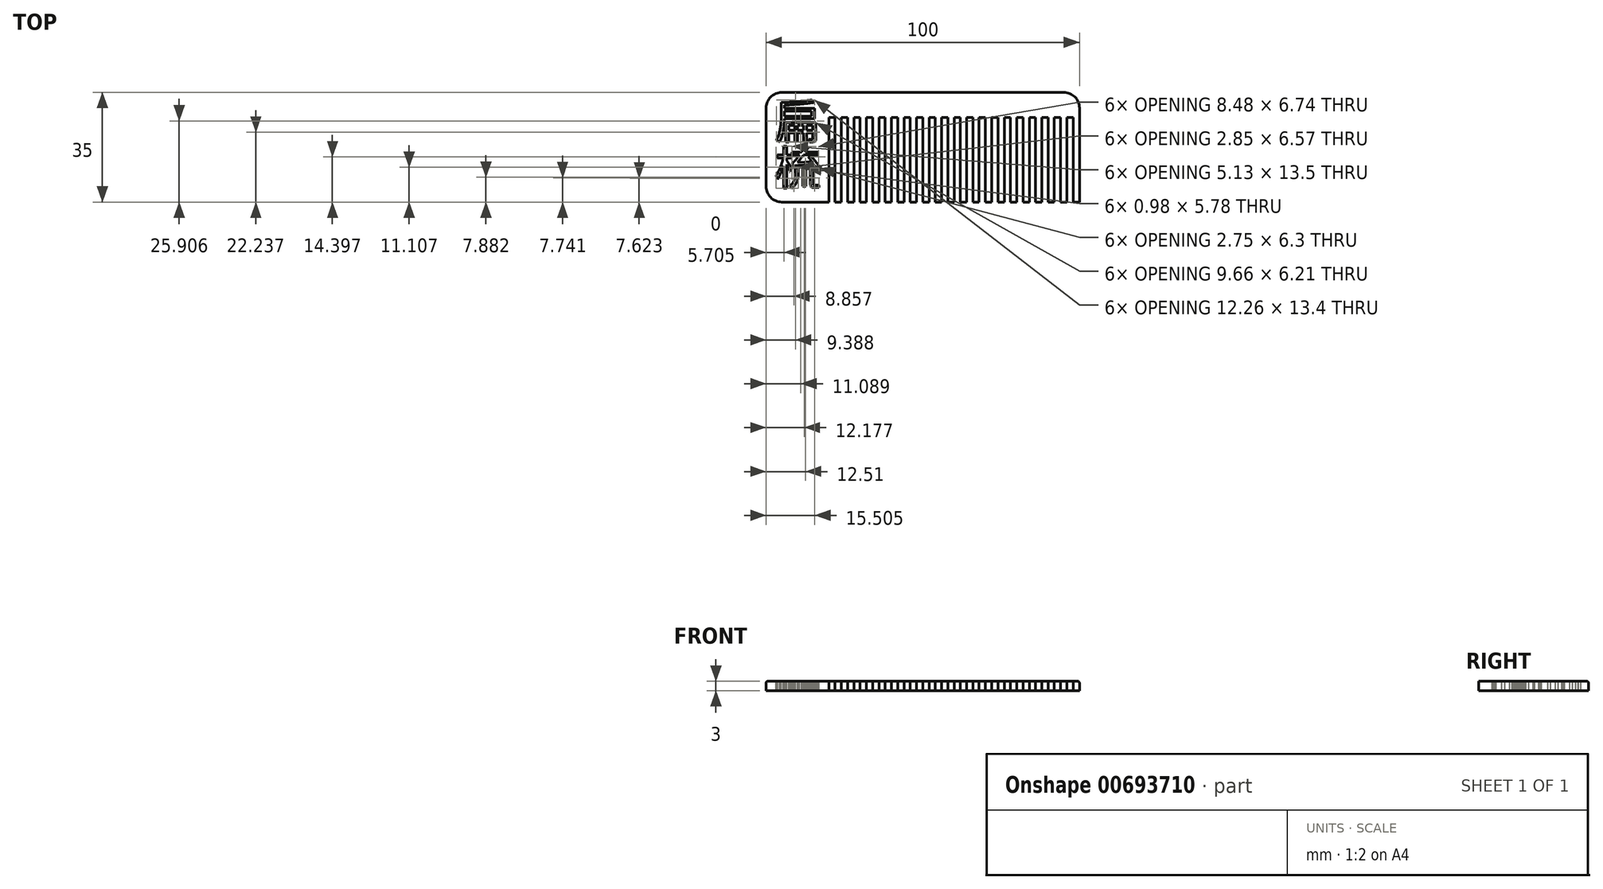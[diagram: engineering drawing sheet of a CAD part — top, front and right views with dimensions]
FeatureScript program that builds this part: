
annotation { "Feature Type Name" : "Feature", "Feature Type Description" : "" }
export const myFeature = defineFeature(function(context is Context, id is Id, definition is map)
    precondition{}
    {
        {
            var Q0;
            Q0=qCreatedBy(makeId("Top.planeOp"),FACE);
            var sketch = newSketch(context, id + "F0", { "sketchPlane" : qUnion([Q0])});
            skLineSegment(sketch, "E0.bottom", {"start": v(50, 17.5) * mm, "end": v(-50, 17.5) * mm});
            skLineSegment(sketch, "E0.top", {"start": v(50, -17.5) * mm, "end": v(-50, -17.5) * mm});
            skLineSegment(sketch, "E0.left", {"start": v(50, 17.5) * mm, "end": v(50, -17.5) * mm});
            skLineSegment(sketch, "E0.right", {"start": v(-50, 17.5) * mm, "end": v(-50, -17.5) * mm});
            skPoint(sketch, "E0.middle", {"position": v(0, 0) * mm});
            skSolve(sketch);
        }
        {
            var Q0;
            Q0 = qSketchRegion(id + "F0", true);
            extrude(context, id + "F1", {"entities" : qUnion([Q0]), "depth" : 3 * mm, "offsetDistance" : 25 * mm});
        }
        {
            var Q0;
            Q0=makeQuery(id+"F1.opExtrude","CAP_FACE",FACE,{"disambiguationData":[OSD([sQuery(id+"F0.wireOp",EDGE,"E0.bottom"),sQuery(id+"F0.wireOp",EDGE,"E0.top"),sQuery(id+"F0.wireOp",EDGE,"E0.left"),sQuery(id+"F0.wireOp",EDGE,"E0.right")])],"isStart":false});
            var sketch = newSketch(context, id + "F2", { "sketchPlane" : qUnion([Q0])});
            skLineSegment(sketch, "E1.bottom", {"start": v(48, 9.5) * mm, "end": v(46, 9.5) * mm});
            skLineSegment(sketch, "E1.top", {"start": v(48, -17.5) * mm, "end": v(46, -17.5) * mm});
            skLineSegment(sketch, "E1.left", {"start": v(48, 9.5) * mm, "end": v(48, -17.5) * mm});
            skLineSegment(sketch, "E1.right", {"start": v(46, 9.5) * mm, "end": v(46, -17.5) * mm});
            skLineSegment(sketch, "E2.1.0.0", {"start": v(42, 9.5) * mm, "end": v(42, -17.5) * mm});
            skLineSegment(sketch, "E2.1.0.1", {"start": v(44, 9.5) * mm, "end": v(44, -17.5) * mm});
            skLineSegment(sketch, "E2.1.0.2", {"start": v(44, -17.5) * mm, "end": v(42, -17.5) * mm});
            skLineSegment(sketch, "E2.1.0.3", {"start": v(44, 9.5) * mm, "end": v(42, 9.5) * mm});
            skLineSegment(sketch, "E2.2.0.0", {"start": v(38, 9.5) * mm, "end": v(38, -17.5) * mm});
            skLineSegment(sketch, "E2.2.0.1", {"start": v(40, 9.5) * mm, "end": v(40, -17.5) * mm});
            skLineSegment(sketch, "E2.2.0.2", {"start": v(40, -17.5) * mm, "end": v(38, -17.5) * mm});
            skLineSegment(sketch, "E2.2.0.3", {"start": v(40, 9.5) * mm, "end": v(38, 9.5) * mm});
            skLineSegment(sketch, "E2.3.0.0", {"start": v(34, 9.5) * mm, "end": v(34, -17.5) * mm});
            skLineSegment(sketch, "E2.3.0.1", {"start": v(36, 9.5) * mm, "end": v(36, -17.5) * mm});
            skLineSegment(sketch, "E2.3.0.2", {"start": v(36, -17.5) * mm, "end": v(34, -17.5) * mm});
            skLineSegment(sketch, "E2.3.0.3", {"start": v(36, 9.5) * mm, "end": v(34, 9.5) * mm});
            skLineSegment(sketch, "E2.4.0.0", {"start": v(30, 9.5) * mm, "end": v(30, -17.5) * mm});
            skLineSegment(sketch, "E2.4.0.1", {"start": v(32, 9.5) * mm, "end": v(32, -17.5) * mm});
            skLineSegment(sketch, "E2.4.0.2", {"start": v(32, -17.5) * mm, "end": v(30, -17.5) * mm});
            skLineSegment(sketch, "E2.4.0.3", {"start": v(32, 9.5) * mm, "end": v(30, 9.5) * mm});
            skLineSegment(sketch, "E2.5.0.0", {"start": v(26, 9.5) * mm, "end": v(26, -17.5) * mm});
            skLineSegment(sketch, "E2.5.0.1", {"start": v(28, 9.5) * mm, "end": v(28, -17.5) * mm});
            skLineSegment(sketch, "E2.5.0.2", {"start": v(28, -17.5) * mm, "end": v(26, -17.5) * mm});
            skLineSegment(sketch, "E2.5.0.3", {"start": v(28, 9.5) * mm, "end": v(26, 9.5) * mm});
            skLineSegment(sketch, "E2.6.0.0", {"start": v(22, 9.5) * mm, "end": v(22, -17.5) * mm});
            skLineSegment(sketch, "E2.6.0.1", {"start": v(24, 9.5) * mm, "end": v(24, -17.5) * mm});
            skLineSegment(sketch, "E2.6.0.2", {"start": v(24, -17.5) * mm, "end": v(22, -17.5) * mm});
            skLineSegment(sketch, "E2.6.0.3", {"start": v(24, 9.5) * mm, "end": v(22, 9.5) * mm});
            skLineSegment(sketch, "E2.7.0.0", {"start": v(18, 9.5) * mm, "end": v(18, -17.5) * mm});
            skLineSegment(sketch, "E2.7.0.1", {"start": v(20, 9.5) * mm, "end": v(20, -17.5) * mm});
            skLineSegment(sketch, "E2.7.0.2", {"start": v(20, -17.5) * mm, "end": v(18, -17.5) * mm});
            skLineSegment(sketch, "E2.7.0.3", {"start": v(20, 9.5) * mm, "end": v(18, 9.5) * mm});
            skLineSegment(sketch, "E2.8.0.0", {"start": v(14, 9.5) * mm, "end": v(14, -17.5) * mm});
            skLineSegment(sketch, "E2.8.0.1", {"start": v(16, 9.5) * mm, "end": v(16, -17.5) * mm});
            skLineSegment(sketch, "E2.8.0.2", {"start": v(16, -17.5) * mm, "end": v(14, -17.5) * mm});
            skLineSegment(sketch, "E2.8.0.3", {"start": v(16, 9.5) * mm, "end": v(14, 9.5) * mm});
            skLineSegment(sketch, "E2.9.0.0", {"start": v(10, 9.5) * mm, "end": v(10, -17.5) * mm});
            skLineSegment(sketch, "E2.9.0.1", {"start": v(12, 9.5) * mm, "end": v(12, -17.5) * mm});
            skLineSegment(sketch, "E2.9.0.2", {"start": v(12, -17.5) * mm, "end": v(10, -17.5) * mm});
            skLineSegment(sketch, "E2.9.0.3", {"start": v(12, 9.5) * mm, "end": v(10, 9.5) * mm});
            skLineSegment(sketch, "E2.10.0.0", {"start": v(6, 9.5) * mm, "end": v(6, -17.5) * mm});
            skLineSegment(sketch, "E2.10.0.1", {"start": v(8, 9.5) * mm, "end": v(8, -17.5) * mm});
            skLineSegment(sketch, "E2.10.0.2", {"start": v(8, -17.5) * mm, "end": v(6, -17.5) * mm});
            skLineSegment(sketch, "E2.10.0.3", {"start": v(8, 9.5) * mm, "end": v(6, 9.5) * mm});
            skLineSegment(sketch, "E2.11.0.0", {"start": v(2, 9.5) * mm, "end": v(2, -17.5) * mm});
            skLineSegment(sketch, "E2.11.0.1", {"start": v(4, 9.5) * mm, "end": v(4, -17.5) * mm});
            skLineSegment(sketch, "E2.11.0.2", {"start": v(4, -17.5) * mm, "end": v(2, -17.5) * mm});
            skLineSegment(sketch, "E2.11.0.3", {"start": v(4, 9.5) * mm, "end": v(2, 9.5) * mm});
            skLineSegment(sketch, "E2.12.0.0", {"start": v(-2, 9.5) * mm, "end": v(-2, -17.5) * mm});
            skLineSegment(sketch, "E2.12.0.1", {"start": v(0, 9.5) * mm, "end": v(0, -17.5) * mm});
            skLineSegment(sketch, "E2.12.0.2", {"start": v(0, -17.5) * mm, "end": v(-2, -17.5) * mm});
            skLineSegment(sketch, "E2.12.0.3", {"start": v(0, 9.5) * mm, "end": v(-2, 9.5) * mm});
            skLineSegment(sketch, "E2.13.0.0", {"start": v(-6, 9.5) * mm, "end": v(-6, -17.5) * mm});
            skLineSegment(sketch, "E2.13.0.1", {"start": v(-4, 9.5) * mm, "end": v(-4, -17.5) * mm});
            skLineSegment(sketch, "E2.13.0.2", {"start": v(-4, -17.5) * mm, "end": v(-6, -17.5) * mm});
            skLineSegment(sketch, "E2.13.0.3", {"start": v(-4, 9.5) * mm, "end": v(-6, 9.5) * mm});
            skLineSegment(sketch, "E2.14.0.0", {"start": v(-10, 9.5) * mm, "end": v(-10, -17.5) * mm});
            skLineSegment(sketch, "E2.14.0.1", {"start": v(-8, 9.5) * mm, "end": v(-8, -17.5) * mm});
            skLineSegment(sketch, "E2.14.0.2", {"start": v(-8, -17.5) * mm, "end": v(-10, -17.5) * mm});
            skLineSegment(sketch, "E2.14.0.3", {"start": v(-8, 9.5) * mm, "end": v(-10, 9.5) * mm});
            skLineSegment(sketch, "E2.15.0.0", {"start": v(-14, 9.5) * mm, "end": v(-14, -17.5) * mm});
            skLineSegment(sketch, "E2.15.0.1", {"start": v(-12, 9.5) * mm, "end": v(-12, -17.5) * mm});
            skLineSegment(sketch, "E2.15.0.2", {"start": v(-12, -17.5) * mm, "end": v(-14, -17.5) * mm});
            skLineSegment(sketch, "E2.15.0.3", {"start": v(-12, 9.5) * mm, "end": v(-14, 9.5) * mm});
            skLineSegment(sketch, "E2.16.0.0", {"start": v(-18, 9.5) * mm, "end": v(-18, -17.5) * mm});
            skLineSegment(sketch, "E2.16.0.1", {"start": v(-16, 9.5) * mm, "end": v(-16, -17.5) * mm});
            skLineSegment(sketch, "E2.16.0.2", {"start": v(-16, -17.5) * mm, "end": v(-18, -17.5) * mm});
            skLineSegment(sketch, "E2.16.0.3", {"start": v(-16, 9.5) * mm, "end": v(-18, 9.5) * mm});
            skLineSegment(sketch, "E2.17.0.0", {"start": v(-22, 9.5) * mm, "end": v(-22, -17.5) * mm});
            skLineSegment(sketch, "E2.17.0.1", {"start": v(-20, 9.5) * mm, "end": v(-20, -17.5) * mm});
            skLineSegment(sketch, "E2.17.0.2", {"start": v(-20, -17.5) * mm, "end": v(-22, -17.5) * mm});
            skLineSegment(sketch, "E2.17.0.3", {"start": v(-20, 9.5) * mm, "end": v(-22, 9.5) * mm});
            skLineSegment(sketch, "E2.18.0.0", {"start": v(-26, 9.5) * mm, "end": v(-26, -17.5) * mm});
            skLineSegment(sketch, "E2.18.0.1", {"start": v(-24, 9.5) * mm, "end": v(-24, -17.5) * mm});
            skLineSegment(sketch, "E2.18.0.2", {"start": v(-24, -17.5) * mm, "end": v(-26, -17.5) * mm});
            skLineSegment(sketch, "E2.18.0.3", {"start": v(-24, 9.5) * mm, "end": v(-26, 9.5) * mm});
            skLineSegment(sketch, "E2.19.0.0", {"start": v(-30, 9.5) * mm, "end": v(-30, -17.5) * mm});
            skLineSegment(sketch, "E2.19.0.1", {"start": v(-28, 9.5) * mm, "end": v(-28, -17.5) * mm});
            skLineSegment(sketch, "E2.19.0.2", {"start": v(-28, -17.5) * mm, "end": v(-30, -17.5) * mm});
            skLineSegment(sketch, "E2.19.0.3", {"start": v(-28, 9.5) * mm, "end": v(-30, 9.5) * mm});
            skLineSegment(sketch, "E2.direction1", {"start": v(46, -17.5) * mm, "end": v(42, -17.5) * mm, "construction": true});
            skSolve(sketch);
        }
        {
            var Q0;
            Q0 = qSketchRegion(id + "F2", true);
            extrude(context, id + "F3", {"entities" : qUnion([Q0]), "operationType" : NewBodyOperationType.REMOVE, "endBound" : BoundingType.THROUGH_ALL, "oppositeDirection" : true, "depth" : 25 * mm, "offsetDistance" : 25 * mm});
        }
        {
            var Q0;
            Q0=makeQuery(id+"F1.opExtrude","CAP_FACE",FACE,{"disambiguationData":[OSD([sQuery(id+"F0.wireOp",EDGE,"E0.bottom"),sQuery(id+"F0.wireOp",EDGE,"E0.top"),sQuery(id+"F0.wireOp",EDGE,"E0.left"),sQuery(id+"F0.wireOp",EDGE,"E0.right")])],"isStart":false});
            var sketch = newSketch(context, id + "F4", { "sketchPlane" : qUnion([Q0])});
            skText(sketch, "E3", { "text": "扁\n梳", "fontName": "NotoSansCJKtc-Regular.otf"});
            const initialGuessF4  = {"E3": [-0.04729, 0.00277, 1, 0, 0.01065]};
            skSetInitialGuess(sketch, initialGuessF4);
            skSolve(sketch);
        }
        {
            var Q0;
            Q0 = qSketchRegion(id + "F4", true);
            extrude(context, id + "F5", {"entities" : qUnion([Q0]), "operationType" : NewBodyOperationType.REMOVE, "endBound" : BoundingType.THROUGH_ALL, "oppositeDirection" : true, "depth" : 25 * mm, "offsetDistance" : 25 * mm});
        }
        {
            var Q0;
            Q0=makeQuery(id+"F1.opExtrude","CAP_EDGE",EDGE,{"disambiguationData":[OSD([sQuery(id+"F0.wireOp",EDGE,"E0.bottom")])],"isStart":false});
            var Q1;
            Q1=makeQuery(id+"F1.opExtrude","CAP_EDGE",EDGE,{"disambiguationData":[OSD([sQuery(id+"F0.wireOp",EDGE,"E0.right")])],"isStart":false});
            var Q2;
            {var subQ0=sQuery(id+"F0.wireOp",EDGE,"E0.right");var subQ1=sQuery(id+"F0.wireOp",EDGE,"E0.top");Q2=makeQuery(id+"F3.boolean.opBoolean","SPLIT",EDGE,{"disambiguationData":[TD([makeQuery(id+"F1.opExtrude","SWEPT_FACE",FACE,{"disambiguationData":[OSD([subQ0])]})])],"derivedFrom":makeQuery(id+"F1.opExtrude","CAP_EDGE",EDGE,{"disambiguationData":[OSD([subQ1])],"isStart":false})});}
            var Q3;
            Q3=makeQuery(id+"F1.opExtrude","CAP_EDGE",EDGE,{"disambiguationData":[OSD([sQuery(id+"F0.wireOp",EDGE,"E0.left")])],"isStart":false});
            var Q4;
            {var subQ0=sQuery(id+"F0.wireOp",EDGE,"E0.top");Q4=makeQuery(id+"F3.boolean.opBoolean","SPLIT",EDGE,{"disambiguationData":[TD([makeQuery(id+"F3.opExtrude","SWEPT_FACE",FACE,{"disambiguationData":[OSD([sQuery(id+"F2.wireOp",EDGE,"E2.18.0.0")])]})])],"derivedFrom":makeQuery(id+"F1.opExtrude","CAP_EDGE",EDGE,{"disambiguationData":[OSD([subQ0])],"isStart":false})});}
            var Q5;
            {var subQ0=sQuery(id+"F0.wireOp",EDGE,"E0.top");Q5=makeQuery(id+"F3.boolean.opBoolean","SPLIT",EDGE,{"disambiguationData":[TD([makeQuery(id+"F3.opExtrude","SWEPT_FACE",FACE,{"disambiguationData":[OSD([sQuery(id+"F2.wireOp",EDGE,"E2.17.0.0")])]})])],"derivedFrom":makeQuery(id+"F1.opExtrude","CAP_EDGE",EDGE,{"disambiguationData":[OSD([subQ0])],"isStart":false})});}
            var Q6;
            {var subQ0=sQuery(id+"F0.wireOp",EDGE,"E0.top");Q6=makeQuery(id+"F3.boolean.opBoolean","SPLIT",EDGE,{"disambiguationData":[TD([makeQuery(id+"F3.opExtrude","SWEPT_FACE",FACE,{"disambiguationData":[OSD([sQuery(id+"F2.wireOp",EDGE,"E2.16.0.0")])]})])],"derivedFrom":makeQuery(id+"F1.opExtrude","CAP_EDGE",EDGE,{"disambiguationData":[OSD([subQ0])],"isStart":false})});}
            var Q7;
            {var subQ0=sQuery(id+"F0.wireOp",EDGE,"E0.top");Q7=makeQuery(id+"F3.boolean.opBoolean","SPLIT",EDGE,{"disambiguationData":[TD([makeQuery(id+"F3.opExtrude","SWEPT_FACE",FACE,{"disambiguationData":[OSD([sQuery(id+"F2.wireOp",EDGE,"E2.15.0.0")])]})])],"derivedFrom":makeQuery(id+"F1.opExtrude","CAP_EDGE",EDGE,{"disambiguationData":[OSD([subQ0])],"isStart":false})});}
            var Q8;
            {var subQ0=sQuery(id+"F0.wireOp",EDGE,"E0.top");Q8=makeQuery(id+"F3.boolean.opBoolean","SPLIT",EDGE,{"disambiguationData":[TD([makeQuery(id+"F3.opExtrude","SWEPT_FACE",FACE,{"disambiguationData":[OSD([sQuery(id+"F2.wireOp",EDGE,"E2.14.0.0")])]})])],"derivedFrom":makeQuery(id+"F1.opExtrude","CAP_EDGE",EDGE,{"disambiguationData":[OSD([subQ0])],"isStart":false})});}
            var Q9;
            {var subQ0=sQuery(id+"F0.wireOp",EDGE,"E0.top");Q9=makeQuery(id+"F3.boolean.opBoolean","SPLIT",EDGE,{"disambiguationData":[TD([makeQuery(id+"F3.opExtrude","SWEPT_FACE",FACE,{"disambiguationData":[OSD([sQuery(id+"F2.wireOp",EDGE,"E2.13.0.0")])]})])],"derivedFrom":makeQuery(id+"F1.opExtrude","CAP_EDGE",EDGE,{"disambiguationData":[OSD([subQ0])],"isStart":false})});}
            var Q10;
            {var subQ0=sQuery(id+"F0.wireOp",EDGE,"E0.top");Q10=makeQuery(id+"F3.boolean.opBoolean","SPLIT",EDGE,{"disambiguationData":[TD([makeQuery(id+"F3.opExtrude","SWEPT_FACE",FACE,{"disambiguationData":[OSD([sQuery(id+"F2.wireOp",EDGE,"E2.12.0.0")])]})])],"derivedFrom":makeQuery(id+"F1.opExtrude","CAP_EDGE",EDGE,{"disambiguationData":[OSD([subQ0])],"isStart":false})});}
            var Q11;
            {var subQ0=sQuery(id+"F0.wireOp",EDGE,"E0.top");Q11=makeQuery(id+"F3.boolean.opBoolean","SPLIT",EDGE,{"disambiguationData":[TD([makeQuery(id+"F3.opExtrude","SWEPT_FACE",FACE,{"disambiguationData":[OSD([sQuery(id+"F2.wireOp",EDGE,"E2.11.0.0")])]})])],"derivedFrom":makeQuery(id+"F1.opExtrude","CAP_EDGE",EDGE,{"disambiguationData":[OSD([subQ0])],"isStart":false})});}
            var Q12;
            {var subQ0=sQuery(id+"F0.wireOp",EDGE,"E0.top");Q12=makeQuery(id+"F3.boolean.opBoolean","SPLIT",EDGE,{"disambiguationData":[TD([makeQuery(id+"F3.opExtrude","SWEPT_FACE",FACE,{"disambiguationData":[OSD([sQuery(id+"F2.wireOp",EDGE,"E2.10.0.0")])]})])],"derivedFrom":makeQuery(id+"F1.opExtrude","CAP_EDGE",EDGE,{"disambiguationData":[OSD([subQ0])],"isStart":false})});}
            var Q13;
            {var subQ0=sQuery(id+"F0.wireOp",EDGE,"E0.top");Q13=makeQuery(id+"F3.boolean.opBoolean","SPLIT",EDGE,{"disambiguationData":[TD([makeQuery(id+"F3.opExtrude","SWEPT_FACE",FACE,{"disambiguationData":[OSD([sQuery(id+"F2.wireOp",EDGE,"E2.9.0.0")])]})])],"derivedFrom":makeQuery(id+"F1.opExtrude","CAP_EDGE",EDGE,{"disambiguationData":[OSD([subQ0])],"isStart":false})});}
            var Q14;
            {var subQ0=sQuery(id+"F0.wireOp",EDGE,"E0.top");Q14=makeQuery(id+"F3.boolean.opBoolean","SPLIT",EDGE,{"disambiguationData":[TD([makeQuery(id+"F3.opExtrude","SWEPT_FACE",FACE,{"disambiguationData":[OSD([sQuery(id+"F2.wireOp",EDGE,"E2.8.0.0")])]})])],"derivedFrom":makeQuery(id+"F1.opExtrude","CAP_EDGE",EDGE,{"disambiguationData":[OSD([subQ0])],"isStart":false})});}
            var Q15;
            {var subQ0=sQuery(id+"F0.wireOp",EDGE,"E0.top");Q15=makeQuery(id+"F3.boolean.opBoolean","SPLIT",EDGE,{"disambiguationData":[TD([makeQuery(id+"F3.opExtrude","SWEPT_FACE",FACE,{"disambiguationData":[OSD([sQuery(id+"F2.wireOp",EDGE,"E2.7.0.0")])]})])],"derivedFrom":makeQuery(id+"F1.opExtrude","CAP_EDGE",EDGE,{"disambiguationData":[OSD([subQ0])],"isStart":false})});}
            var Q16;
            {var subQ0=sQuery(id+"F0.wireOp",EDGE,"E0.top");Q16=makeQuery(id+"F3.boolean.opBoolean","SPLIT",EDGE,{"disambiguationData":[TD([makeQuery(id+"F3.opExtrude","SWEPT_FACE",FACE,{"disambiguationData":[OSD([sQuery(id+"F2.wireOp",EDGE,"E2.6.0.0")])]})])],"derivedFrom":makeQuery(id+"F1.opExtrude","CAP_EDGE",EDGE,{"disambiguationData":[OSD([subQ0])],"isStart":false})});}
            var Q17;
            {var subQ0=sQuery(id+"F0.wireOp",EDGE,"E0.top");Q17=makeQuery(id+"F3.boolean.opBoolean","SPLIT",EDGE,{"disambiguationData":[TD([makeQuery(id+"F3.opExtrude","SWEPT_FACE",FACE,{"disambiguationData":[OSD([sQuery(id+"F2.wireOp",EDGE,"E2.5.0.0")])]})])],"derivedFrom":makeQuery(id+"F1.opExtrude","CAP_EDGE",EDGE,{"disambiguationData":[OSD([subQ0])],"isStart":false})});}
            var Q18;
            {var subQ0=sQuery(id+"F0.wireOp",EDGE,"E0.top");Q18=makeQuery(id+"F3.boolean.opBoolean","SPLIT",EDGE,{"disambiguationData":[TD([makeQuery(id+"F3.opExtrude","SWEPT_FACE",FACE,{"disambiguationData":[OSD([sQuery(id+"F2.wireOp",EDGE,"E2.4.0.0")])]})])],"derivedFrom":makeQuery(id+"F1.opExtrude","CAP_EDGE",EDGE,{"disambiguationData":[OSD([subQ0])],"isStart":false})});}
            var Q19;
            {var subQ0=sQuery(id+"F0.wireOp",EDGE,"E0.top");Q19=makeQuery(id+"F3.boolean.opBoolean","SPLIT",EDGE,{"disambiguationData":[TD([makeQuery(id+"F3.opExtrude","SWEPT_FACE",FACE,{"disambiguationData":[OSD([sQuery(id+"F2.wireOp",EDGE,"E2.3.0.0")])]})])],"derivedFrom":makeQuery(id+"F1.opExtrude","CAP_EDGE",EDGE,{"disambiguationData":[OSD([subQ0])],"isStart":false})});}
            var Q20;
            {var subQ0=sQuery(id+"F0.wireOp",EDGE,"E0.top");Q20=makeQuery(id+"F3.boolean.opBoolean","SPLIT",EDGE,{"disambiguationData":[TD([makeQuery(id+"F3.opExtrude","SWEPT_FACE",FACE,{"disambiguationData":[OSD([sQuery(id+"F2.wireOp",EDGE,"E2.2.0.0")])]})])],"derivedFrom":makeQuery(id+"F1.opExtrude","CAP_EDGE",EDGE,{"disambiguationData":[OSD([subQ0])],"isStart":false})});}
            var Q21;
            {var subQ0=sQuery(id+"F0.wireOp",EDGE,"E0.top");Q21=makeQuery(id+"F3.boolean.opBoolean","SPLIT",EDGE,{"disambiguationData":[TD([makeQuery(id+"F3.opExtrude","SWEPT_FACE",FACE,{"disambiguationData":[OSD([sQuery(id+"F2.wireOp",EDGE,"E2.1.0.0")])]})])],"derivedFrom":makeQuery(id+"F1.opExtrude","CAP_EDGE",EDGE,{"disambiguationData":[OSD([subQ0])],"isStart":false})});}
            var Q22;
            {var subQ0=sQuery(id+"F0.wireOp",EDGE,"E0.top");Q22=makeQuery(id+"F3.boolean.opBoolean","SPLIT",EDGE,{"disambiguationData":[TD([makeQuery(id+"F3.opExtrude","SWEPT_FACE",FACE,{"disambiguationData":[OSD([sQuery(id+"F2.wireOp",EDGE,"E1.right")])]})])],"derivedFrom":makeQuery(id+"F1.opExtrude","CAP_EDGE",EDGE,{"disambiguationData":[OSD([subQ0])],"isStart":false})});}
            fillet(context, id + "F6", {"entities" : qUnion([Q0, Q1, Q2, Q3, Q4, Q5, Q6, Q7, Q8, Q9, Q10, Q11, Q12, Q13, Q14, Q15, Q16, Q17, Q18, Q19, Q20, Q21, Q22]), "radius" : 0.5 * mm, "tangentPropagation" : true, "allowEdgeOverflow" : false});
        }
        {
            var Q0;
            Q0=makeQuery(id+"F6.opFillet","BLEND_EDGE",EDGE,{"blendedFrom":[makeQuery(id+"F1.opExtrude","CAP_EDGE",EDGE,{"disambiguationData":[OSD([sQuery(id+"F0.wireOp",EDGE,"E0.bottom")])],"isStart":false}),makeQuery(id+"F1.opExtrude","CAP_EDGE",EDGE,{"disambiguationData":[OSD([sQuery(id+"F0.wireOp",EDGE,"E0.right")])],"isStart":false})],"blendedInto":[]});
            var Q1;
            {var subQ0=sQuery(id+"F0.wireOp",EDGE,"E0.right");var subQ1=sQuery(id+"F0.wireOp",EDGE,"E0.top");Q1=makeQuery(id+"F6.opFillet","BLEND_EDGE",EDGE,{"blendedFrom":[makeQuery(id+"F1.opExtrude","CAP_EDGE",EDGE,{"disambiguationData":[OSD([subQ0])],"isStart":false}),makeQuery(id+"F3.boolean.opBoolean","SPLIT",EDGE,{"disambiguationData":[TD([makeQuery(id+"F1.opExtrude","SWEPT_FACE",FACE,{"disambiguationData":[OSD([subQ0])]})])],"derivedFrom":makeQuery(id+"F1.opExtrude","CAP_EDGE",EDGE,{"disambiguationData":[OSD([subQ1])],"isStart":false})})],"blendedInto":[]});}
            var Q2;
            Q2=makeQuery(id+"F6.opFillet","BLEND_EDGE",EDGE,{"blendedFrom":[makeQuery(id+"F1.opExtrude","CAP_EDGE",EDGE,{"disambiguationData":[OSD([sQuery(id+"F0.wireOp",EDGE,"E0.bottom")])],"isStart":false}),makeQuery(id+"F1.opExtrude","CAP_EDGE",EDGE,{"disambiguationData":[OSD([sQuery(id+"F0.wireOp",EDGE,"E0.left")])],"isStart":false})],"blendedInto":[]});
            fillet(context, id + "F7", {"entities" : qUnion([Q0, Q1, Q2]), "radius" : 5 * mm, "tangentPropagation" : true, "allowEdgeOverflow" : false});
        }
    });
